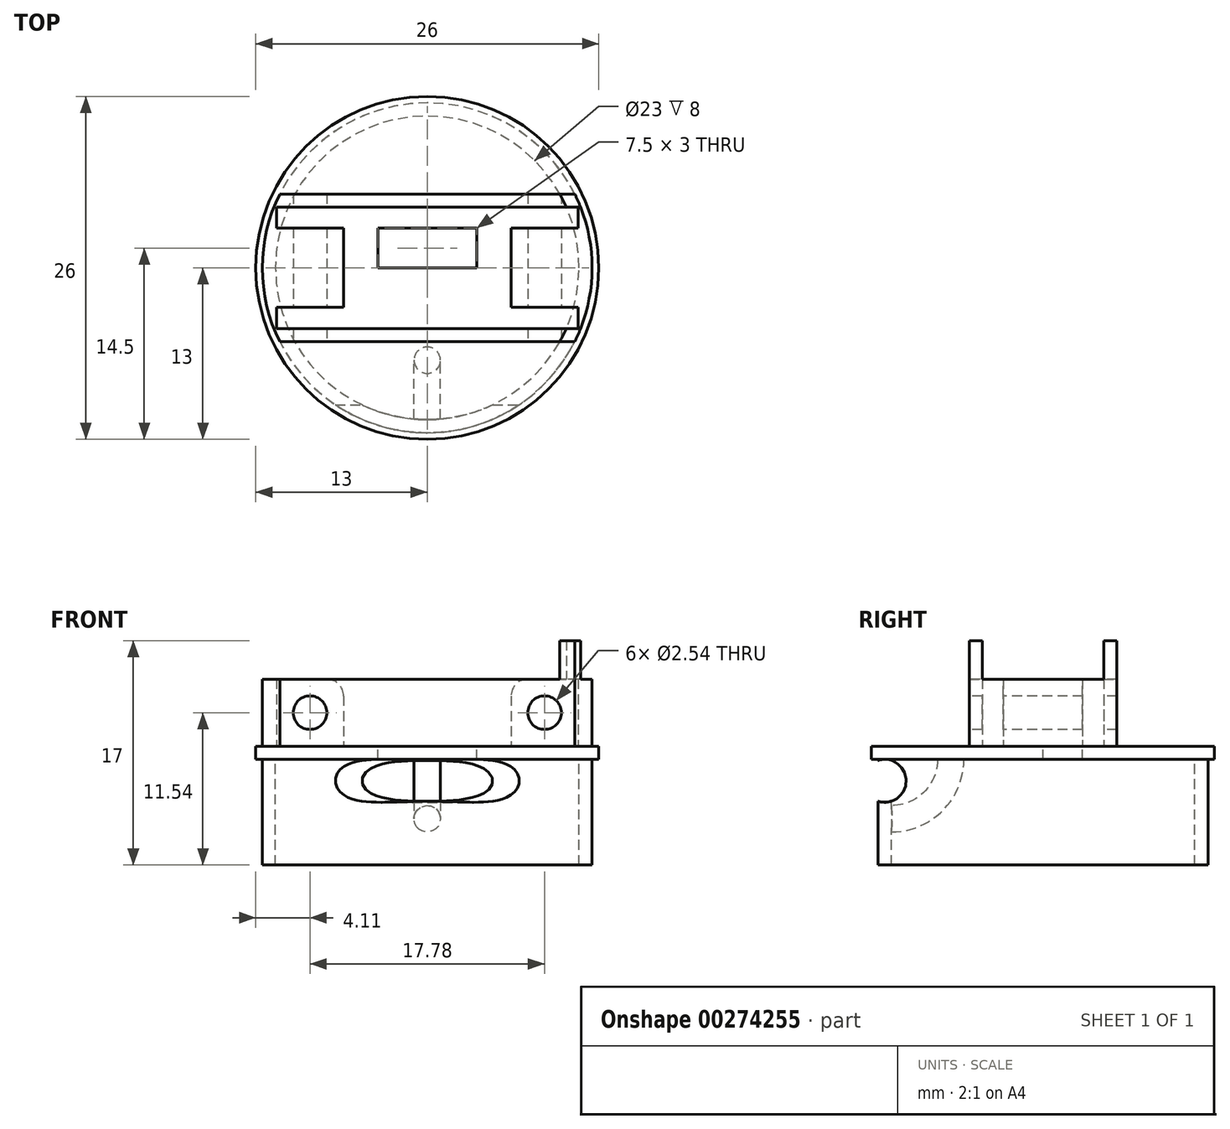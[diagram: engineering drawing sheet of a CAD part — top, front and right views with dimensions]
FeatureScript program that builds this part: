
annotation { "Feature Type Name" : "Feature", "Feature Type Description" : "" }
export const myFeature = defineFeature(function(context is Context, id is Id, definition is map)
    precondition{}
    {
        {
            var Q0;
            Q0=qCreatedBy(makeId("Top.planeOp"),FACE);
            var sketch = newSketch(context, id + "F0", { "sketchPlane" : qUnion([Q0])});
            skCircle(sketch, "E0", {"center": v(0, 0) * mm, "radius": 4.6 * mm, "construction": true});
            skLineSegment(sketch, "E1", {"start": v(11.62, -4.6) * mm, "end": v(11.43, -4.6) * mm});
            skLineSegment(sketch, "E2", {"start": v(-11.62, 4.6) * mm, "end": v(-11.43, 4.6) * mm});
            skCircle(sketch, "E3", {"center": v(0, 0) * mm, "radius": 12.5 * mm});
            skLineSegment(sketch, "E4", {"start": v(0, 0) * mm, "end": v(3.75, 0) * mm});
            skLineSegment(sketch, "E5", {"start": v(0, 0) * mm, "end": v(-3.75, 0) * mm});
            skLineSegment(sketch, "E6", {"start": v(11.43, 3) * mm, "end": v(-11.43, 3) * mm});
            skLineSegment(sketch, "E7", {"start": v(-11.43, 3) * mm, "end": v(-11.43, 0) * mm});
            skLineSegment(sketch, "E8", {"start": v(-11.43, 3) * mm, "end": v(-11.43, 4.6) * mm});
            skLineSegment(sketch, "E9", {"start": v(11.43, 3) * mm, "end": v(11.43, 0) * mm});
            skLineSegment(sketch, "E10", {"start": v(11.43, 3) * mm, "end": v(11.43, 4.6) * mm});
            skLineSegment(sketch, "E11", {"start": v(11.43, 0) * mm, "end": v(11.43, -3) * mm});
            skLineSegment(sketch, "E12", {"start": v(11.43, -3) * mm, "end": v(11.43, -4.6) * mm});
            skLineSegment(sketch, "E13", {"start": v(11.43, -3) * mm, "end": v(6.35, -3) * mm});
            skLineSegment(sketch, "E14", {"start": v(-11.43, -3) * mm, "end": v(-11.43, 0) * mm});
            skLineSegment(sketch, "E15", {"start": v(-11.43, -3) * mm, "end": v(-11.43, -4.6) * mm});
            skLineSegment(sketch, "E16", {"start": v(-11.18, -5.6) * mm, "end": v(11.18, -5.6) * mm});
            skLineSegment(sketch, "E17", {"start": v(-11.18, 5.6) * mm, "end": v(11.18, 5.6) * mm});
            skCircle(sketch, "E18", {"center": v(0, 0) * mm, "radius": 11.5 * mm});
            skCircle(sketch, "E19", {"center": v(0, 0) * mm, "radius": 13 * mm});
            skLineSegment(sketch, "E20", {"start": v(-3.75, 3) * mm, "end": v(-3.75, 0) * mm});
            skLineSegment(sketch, "E21", {"start": v(3.75, 0) * mm, "end": v(3.75, 3) * mm});
            skLineSegment(sketch, "E22", {"start": v(6.35, 3) * mm, "end": v(6.35, 0) * mm});
            skLineSegment(sketch, "E23", {"start": v(-6.35, 3) * mm, "end": v(-6.35, 0) * mm});
            skLineSegment(sketch, "E24", {"start": v(0, -3) * mm, "end": v(-6.35, -3) * mm});
            skLineSegment(sketch, "E25", {"start": v(6.35, -3) * mm, "end": v(6.35, -3) * mm});
            skLineSegment(sketch, "E26", {"start": v(-6.35, -3) * mm, "end": v(-11.43, -3) * mm});
            skLineSegment(sketch, "E27", {"start": v(6.35, -3) * mm, "end": v(0, -3) * mm});
            skLineSegment(sketch, "E28", {"start": v(3.75, 0) * mm, "end": v(6.35, 0) * mm});
            skLineSegment(sketch, "E29", {"start": v(-3.75, 0) * mm, "end": v(-6.35, 0) * mm});
            skLineSegment(sketch, "E30", {"start": v(6.35, 0) * mm, "end": v(6.35, -3) * mm});
            skLineSegment(sketch, "E31", {"start": v(6.35, 0) * mm, "end": v(11.43, 0) * mm});
            skLineSegment(sketch, "E32", {"start": v(-6.35, 0) * mm, "end": v(-6.35, -3) * mm});
            skLineSegment(sketch, "E33", {"start": v(-6.35, 0) * mm, "end": v(-11.43, 0) * mm});
            skLineSegment(sketch, "E34", {"start": v(11.43, 4.6) * mm, "end": v(11.43, 4.6) * mm});
            skLineSegment(sketch, "E35", {"start": v(-11.43, 4.6) * mm, "end": v(11.43, 4.6) * mm});
            skLineSegment(sketch, "E36", {"start": v(-11.43, -4.6) * mm, "end": v(-11.43, -4.6) * mm});
            skLineSegment(sketch, "E37", {"start": v(11.43, -4.6) * mm, "end": v(11.43, -4.6) * mm});
            skLineSegment(sketch, "E38", {"start": v(11.43, -4.6) * mm, "end": v(-11.43, -4.6) * mm});
            skLineSegment(sketch, "E39", {"start": v(11.43, 4.6) * mm, "end": v(11.62, 4.6) * mm});
            skLineSegment(sketch, "E40", {"start": v(-11.43, 4.6) * mm, "end": v(-11.43, 4.6) * mm});
            skLineSegment(sketch, "E41", {"start": v(-11.43, -4.6) * mm, "end": v(-11.62, -4.6) * mm});
            skSolve(sketch);
        }
        {
            var Q0;
            {var subQ0=sQuery(id+"F0.wireOp",EDGE,"E17");var subQ1=sQuery(id+"F0.wireOp",EDGE,"E3");var subQ2=makeQuery(id+"F0.imprint","INTERSECT",VERTEX,{"disambiguationData":[OD(0.0)],"derivedFrom":[subQ1,subQ0]});Q0=makeQuery(id+"F0.imprint","IMPRINT",FACE,{"disambiguationData":[TD([[makeQuery(id+"F0.imprint","IMPRINT",EDGE,{"disambiguationData":[TD([[subQ2,1.0]])],"derivedFrom":subQ1}),1.0]])]});}
            var Q1;
            {var subQ0=sQuery(id+"F0.wireOp",EDGE,"E16");var subQ1=sQuery(id+"F0.wireOp",EDGE,"E3");var subQ2=makeQuery(id+"F0.imprint","INTERSECT",VERTEX,{"disambiguationData":[OD(0.0)],"derivedFrom":[subQ1,subQ0]});Q1=makeQuery(id+"F0.imprint","IMPRINT",FACE,{"disambiguationData":[TD([[makeQuery(id+"F0.imprint","IMPRINT",EDGE,{"disambiguationData":[TD([[subQ2,-1.0]])],"derivedFrom":subQ1}),1.0]])]});}
            extrude(context, id + "F1", {"entities" : qUnion([Q0, Q1]), "depth" : 8 * mm});
        }
        {
            var Q0;
            {var subQ0=sQuery(id+"F0.wireOp",EDGE,"E18");var subQ1=sQuery(id+"F0.wireOp",EDGE,"E16");var subQ2=makeQuery(id+"F0.imprint","INTERSECT",VERTEX,{"disambiguationData":[OD(0.0)],"derivedFrom":[subQ1,subQ0]});Q0=makeQuery(id+"F0.imprint","IMPRINT",FACE,{"disambiguationData":[TD([[makeQuery(id+"F0.imprint","IMPRINT",EDGE,{"disambiguationData":[TD([[subQ2,-1.0]])],"derivedFrom":subQ1}),1.0]])]});}
            var Q1;
            {var subQ0=sQuery(id+"F0.wireOp",EDGE,"E18");var subQ1=sQuery(id+"F0.wireOp",EDGE,"E17");var subQ2=makeQuery(id+"F0.imprint","INTERSECT",VERTEX,{"disambiguationData":[OD(0.0)],"derivedFrom":[subQ1,subQ0]});Q1=makeQuery(id+"F0.imprint","IMPRINT",FACE,{"disambiguationData":[TD([[makeQuery(id+"F0.imprint","IMPRINT",EDGE,{"disambiguationData":[TD([[subQ2,-1.0]])],"derivedFrom":subQ1}),-1.0]])]});}
            var Q2;
            {var subQ5=sQuery(id+"F0.wireOp",EDGE,"E30");Q2=makeQuery(id+"F0.imprint","IMPRINT",FACE,{"disambiguationData":[TD([[makeQuery(id+"F0.imprint","IMPRINT",EDGE,{"derivedFrom":subQ5}),1.0]])]});}
            var Q3;
            {var subQ5=sQuery(id+"F0.wireOp",EDGE,"E22");Q3=makeQuery(id+"F0.imprint","IMPRINT",FACE,{"disambiguationData":[TD([[makeQuery(id+"F0.imprint","IMPRINT",EDGE,{"derivedFrom":subQ5}),1.0]])]});}
            var Q4;
            {var subQ1=sQuery(id+"F0.wireOp",EDGE,"E6");var subQ3=sQuery(id+"F0.wireOp",EDGE,"E18");var subQ4=makeQuery(id+"F0.imprint","INTERSECT",VERTEX,{"disambiguationData":[OD(0.0)],"derivedFrom":[subQ1,subQ3]});Q4=makeQuery(id+"F0.imprint","IMPRINT",FACE,{"disambiguationData":[TD([[makeQuery(id+"F0.imprint","IMPRINT",EDGE,{"disambiguationData":[TD([[subQ4,1.0]])],"derivedFrom":subQ3}),-1.0]])]});}
            var Q5;
            {var subQ1=sQuery(id+"F0.wireOp",EDGE,"E11");var subQ3=sQuery(id+"F0.wireOp",EDGE,"E18");var subQ4=makeQuery(id+"F0.imprint","INTERSECT",VERTEX,{"derivedFrom":[subQ1,subQ3]});Q5=makeQuery(id+"F0.imprint","IMPRINT",FACE,{"disambiguationData":[TD([[makeQuery(id+"F0.imprint","IMPRINT",EDGE,{"disambiguationData":[TD([[subQ4,1.0]])],"derivedFrom":subQ3}),-1.0]])]});}
            var Q6;
            {var subQ1=sQuery(id+"F0.wireOp",EDGE,"E14");var subQ3=sQuery(id+"F0.wireOp",EDGE,"E18");var subQ4=makeQuery(id+"F0.imprint","INTERSECT",VERTEX,{"derivedFrom":[subQ1,subQ3]});Q6=makeQuery(id+"F0.imprint","IMPRINT",FACE,{"disambiguationData":[TD([[makeQuery(id+"F0.imprint","IMPRINT",EDGE,{"disambiguationData":[TD([[subQ4,-1.0]])],"derivedFrom":subQ3}),-1.0]])]});}
            var Q7;
            {var subQ0=sQuery(id+"F0.wireOp",EDGE,"E32");Q7=makeQuery(id+"F0.imprint","IMPRINT",FACE,{"disambiguationData":[TD([[makeQuery(id+"F0.imprint","IMPRINT",EDGE,{"derivedFrom":subQ0}),-1.0]])]});}
            var Q8;
            {var subQ1=sQuery(id+"F0.wireOp",EDGE,"E6");var subQ3=sQuery(id+"F0.wireOp",EDGE,"E18");var subQ4=makeQuery(id+"F0.imprint","INTERSECT",VERTEX,{"disambiguationData":[OD(1.0)],"derivedFrom":[subQ1,subQ3]});Q8=makeQuery(id+"F0.imprint","IMPRINT",FACE,{"disambiguationData":[TD([[makeQuery(id+"F0.imprint","IMPRINT",EDGE,{"disambiguationData":[TD([[subQ4,-1.0]])],"derivedFrom":subQ3}),-1.0]])]});}
            var Q9;
            {var subQ6=sQuery(id+"F0.wireOp",EDGE,"E23");Q9=makeQuery(id+"F0.imprint","IMPRINT",FACE,{"disambiguationData":[TD([[makeQuery(id+"F0.imprint","IMPRINT",EDGE,{"derivedFrom":subQ6}),-1.0]])]});}
            var Q10;
            {var subQ2=sQuery(id+"F0.wireOp",EDGE,"E2");Q10=makeQuery(id+"F0.imprint","IMPRINT",FACE,{"disambiguationData":[TD([[makeQuery(id+"F0.imprint","IMPRINT",EDGE,{"derivedFrom":subQ2}),-1.0]])]});}
            var Q11;
            {var subQ7=sQuery(id+"F0.wireOp",EDGE,"E1");Q11=makeQuery(id+"F0.imprint","IMPRINT",FACE,{"disambiguationData":[TD([[makeQuery(id+"F0.imprint","IMPRINT",EDGE,{"derivedFrom":subQ7}),-1.0]])]});}
            var Q12;
            {var subQ1=sQuery(id+"F0.wireOp",EDGE,"E9");var subQ3=sQuery(id+"F0.wireOp",EDGE,"E18");var subQ4=makeQuery(id+"F0.imprint","INTERSECT",VERTEX,{"derivedFrom":[subQ1,subQ3]});Q12=makeQuery(id+"F0.imprint","IMPRINT",FACE,{"disambiguationData":[TD([[makeQuery(id+"F0.imprint","IMPRINT",EDGE,{"disambiguationData":[TD([[subQ4,1.0]])],"derivedFrom":subQ3}),1.0]])]});}
            var Q13;
            {var subQ1=sQuery(id+"F0.wireOp",EDGE,"E7");var subQ3=sQuery(id+"F0.wireOp",EDGE,"E18");var subQ4=makeQuery(id+"F0.imprint","INTERSECT",VERTEX,{"derivedFrom":[subQ1,subQ3]});Q13=makeQuery(id+"F0.imprint","IMPRINT",FACE,{"disambiguationData":[TD([[makeQuery(id+"F0.imprint","IMPRINT",EDGE,{"disambiguationData":[TD([[subQ4,-1.0]])],"derivedFrom":subQ3}),1.0]])]});}
            var Q14;
            {var subQ1=sQuery(id+"F0.wireOp",EDGE,"E2");Q14=makeQuery(id+"F0.imprint","IMPRINT",FACE,{"disambiguationData":[TD([[makeQuery(id+"F0.imprint","IMPRINT",EDGE,{"derivedFrom":subQ1}),1.0]])]});}
            var Q15;
            {var subQ0=sQuery(id+"F0.wireOp",EDGE,"E41");Q15=makeQuery(id+"F0.imprint","IMPRINT",FACE,{"disambiguationData":[TD([[makeQuery(id+"F0.imprint","IMPRINT",EDGE,{"derivedFrom":subQ0}),1.0]])]});}
            var Q16;
            {var subQ7=sQuery(id+"F0.wireOp",EDGE,"E1");Q16=makeQuery(id+"F0.imprint","IMPRINT",FACE,{"disambiguationData":[TD([[makeQuery(id+"F0.imprint","IMPRINT",EDGE,{"derivedFrom":subQ7}),1.0]])]});}
            var Q17;
            {var subQ0=sQuery(id+"F0.wireOp",EDGE,"E39");Q17=makeQuery(id+"F0.imprint","IMPRINT",FACE,{"disambiguationData":[TD([[makeQuery(id+"F0.imprint","IMPRINT",EDGE,{"derivedFrom":subQ0}),1.0]])]});}
            extrude(context, id + "F2", {"entities" : qUnion([Q0, Q1, Q2, Q3, Q4, Q5, Q6, Q7, Q8, Q9, Q10, Q11, Q12, Q13, Q14, Q15, Q16, Q17]), "operationType" : NewBodyOperationType.ADD, "depth" : 5.08 * mm});
        }
        {
            var Q0;
            Q0=qCreatedBy(makeId("Top.planeOp"),FACE);
            var sketch = newSketch(context, id + "F3", { "sketchPlane" : qUnion([Q0])});
            skCircle(sketch, "E42", {"center": v(0, 0) * mm, "radius": 12.5 * mm});
            skCircle(sketch, "E43", {"center": v(0, 0) * mm, "radius": 11.5 * mm});
            skCircle(sketch, "E44", {"center": v(0, 0) * mm, "radius": 13 * mm});
            skSolve(sketch);
        }
        {
            var Q0;
            Q0=makeQuery(id+"F3.imprint","IMPRINT",FACE,{"disambiguationData":[TD([[makeQuery(id+"F3.imprint","IMPRINT",EDGE,{"derivedFrom":sQuery(id+"F3.wireOp",EDGE,"E42")}),-1.0]])]});
            var Q1;
            Q1=makeQuery(id+"F3.imprint","IMPRINT",FACE,{"disambiguationData":[TD([[makeQuery(id+"F3.imprint","IMPRINT",EDGE,{"derivedFrom":sQuery(id+"F3.wireOp",EDGE,"E43")}),1.0]])]});
            var Q2;
            Q2=makeQuery(id+"F3.imprint","IMPRINT",FACE,{"disambiguationData":[TD([[makeQuery(id+"F3.imprint","IMPRINT",EDGE,{"derivedFrom":sQuery(id+"F3.wireOp",EDGE,"E42")}),1.0]])]});
            extrude(context, id + "F4", {"entities" : qUnion([Q0, Q1, Q2]), "operationType" : NewBodyOperationType.ADD, "oppositeDirection" : true, "depth" : 1 * mm});
        }
        {
            var Q0;
            Q0=makeQuery(id+"F3.imprint","IMPRINT",FACE,{"disambiguationData":[TD([[makeQuery(id+"F3.imprint","IMPRINT",EDGE,{"derivedFrom":sQuery(id+"F3.wireOp",EDGE,"E42")}),1.0]])]});
            extrude(context, id + "F5", {"entities" : qUnion([Q0]), "operationType" : NewBodyOperationType.ADD, "oppositeDirection" : true, "depth" : 9 * mm});
        }
        {
            var Q0;
            Q0=makeQuery(id+"F0.imprint","IMPRINT",FACE,{"disambiguationData":[TD([[makeQuery(id+"F0.imprint","IMPRINT",EDGE,{"derivedFrom":sQuery(id+"F0.wireOp",EDGE,"E4")}),1.0]])]});
            extrude(context, id + "F6", {"entities" : qUnion([Q0]), "operationType" : NewBodyOperationType.REMOVE, "endBound" : BoundingType.THROUGH_ALL, "oppositeDirection" : true, "depth" : 25 * mm});
        }
        {
            var Q0;
            Q0=qCreatedBy(makeId("Right.planeOp"),FACE);
            var sketch = newSketch(context, id + "F7", { "sketchPlane" : qUnion([Q0])});
            skCircle(sketch, "E45", {"center": v(-12, -2.62) * mm, "radius": 1.63 * mm});
            skLineSegment(sketch, "E46", {"start": v(-12, -2.62) * mm, "end": v(-12, 0) * mm, "construction": true});
            skSolve(sketch);
        }
        {
            var Q0;
            Q0 = qSketchRegion(id + "F7", true);
            extrude(context, id + "F8", {"entities" : qUnion([Q0]), "operationType" : NewBodyOperationType.REMOVE, "endBound" : BoundingType.SYMMETRIC, "oppositeDirection" : true, "depth" : 25 * mm});
        }
        {
            var Q0;
            Q0=makeQuery(id+"F4.boolean.opBoolean","SPLIT",FACE,{"disambiguationData":[TD([makeQuery(id+"F5.opExtrude","SWEPT_FACE",FACE,{"disambiguationData":[OSD([sQuery(id+"F3.wireOp",EDGE,"E43")])]})])],"derivedFrom":makeQuery(id+"F4.opExtrude","CAP_FACE",FACE,{"disambiguationData":[OSD([sQuery(id+"F3.wireOp",EDGE,"E44")])],"isStart":false})});
            var sketch = newSketch(context, id + "F9", { "sketchPlane" : qUnion([Q0])});
            skLineSegment(sketch, "E47.bottom", {"start": v(0.75, 11.5) * mm, "end": v(-0.75, 11.5) * mm});
            skPoint(sketch, "E47.middle", {"position": v(0, 9.5) * mm});
            skCircle(sketch, "E48", {"center": v(0, 7) * mm, "radius": 1 * mm});
            skLineSegment(sketch, "E49", {"start": v(0, 7) * mm, "end": v(0, 11.5) * mm, "construction": true});
            skSolve(sketch);
        }
        {
            var Q0;
            Q0 = qSketchRegion(id + "F9", true);
            var Q1;
            Q1=sQuery(id+"F9.wireOp",EDGE,"E47.bottom");
            revolve(context, id + "F10", {"operationType" : NewBodyOperationType.ADD, "entities" : qUnion([Q0]), "axis" : qUnion([Q1]), "revolveType" : RevolveType.ONE_DIRECTION, "angle" : 90 * degree});
        }
        {
            var Q0;
            Q0=qCreatedBy(makeId("Front.planeOp"),FACE);
            var sketch = newSketch(context, id + "F11", { "sketchPlane" : qUnion([Q0])});
            skLineSegment(sketch, "E50", {"start": v(-8.9, 0) * mm, "end": v(-8.9, 2.54) * mm, "construction": true});
            skLineSegment(sketch, "E51", {"start": v(-8.9, 0) * mm, "end": v(0, 0) * mm, "construction": true});
            skLineSegment(sketch, "E52", {"start": v(8.9, 0) * mm, "end": v(8.9, 2.54) * mm, "construction": true});
            skCircle(sketch, "E53", {"center": v(8.9, 2.54) * mm, "radius": 1.27 * mm});
            skCircle(sketch, "E54", {"center": v(-8.9, 2.54) * mm, "radius": 1.27 * mm});
            skCircle(sketch, "E55", {"center": v(-8.9, 2.54) * mm, "radius": 2.54 * mm, "construction": true});
            skCircle(sketch, "E56", {"center": v(8.9, 2.54) * mm, "radius": 2.54 * mm, "construction": true});
            skLineSegment(sketch, "E57", {"start": v(0, 0) * mm, "end": v(8.9, 0) * mm, "construction": true});
            skSolve(sketch);
        }
        {
            var Q0;
            Q0=makeQuery(id+"F11.imprint","IMPRINT",FACE,{"disambiguationData":[TD([[makeQuery(id+"F11.imprint","IMPRINT",EDGE,{"derivedFrom":sQuery(id+"F11.wireOp",EDGE,"E54")}),1.0]])]});
            var Q1;
            Q1=makeQuery(id+"F11.imprint","IMPRINT",FACE,{"disambiguationData":[TD([[makeQuery(id+"F11.imprint","IMPRINT",EDGE,{"derivedFrom":sQuery(id+"F11.wireOp",EDGE,"E53")}),1.0]])]});
            extrude(context, id + "F12", {"entities" : qUnion([Q0, Q1]), "operationType" : NewBodyOperationType.REMOVE, "endBound" : BoundingType.SYMMETRIC, "oppositeDirection" : true, "depth" : 50 * mm});
        }
        {
            var Q0;
            Q0=makeQuery(id+"F2.opExtrude","CAP_EDGE",EDGE,{"disambiguationData":[OSD([sQuery(id+"F0.wireOp",EDGE,"E22"),sQuery(id+"F0.wireOp",EDGE,"E30")])],"isStart":false});
            var Q1;
            Q1=makeQuery(id+"F2.opExtrude","CAP_EDGE",EDGE,{"disambiguationData":[OSD([sQuery(id+"F0.wireOp",EDGE,"E23"),sQuery(id+"F0.wireOp",EDGE,"E32")])],"isStart":false});
            fillet(context, id + "F13", {"entities" : qUnion([Q0, Q1]), "radius" : 1.27 * mm, "tangentPropagation" : true, "allowEdgeOverflow" : false});
        }
        {
            var Q0;
            Q0=makeQuery(id+"F3.imprint","IMPRINT",FACE,{"disambiguationData":[TD([[makeQuery(id+"F3.imprint","IMPRINT",EDGE,{"derivedFrom":sQuery(id+"F3.wireOp",EDGE,"E43")}),1.0]])]});
            var sketch = newSketch(context, id + "F14", { "sketchPlane" : qUnion([Q0])});
            skLineSegment(sketch, "E58", {"start": v(0, 12) * mm, "end": v(0.5, 12.5) * mm});
            skLineSegment(sketch, "E59", {"start": v(0.5, 12.5) * mm, "end": v(-0.5, 12.5) * mm});
            skLineSegment(sketch, "E60", {"start": v(-0.5, 12.5) * mm, "end": v(0, 12) * mm});
            skLineSegment(sketch, "E61", {"start": v(0, -11.5) * mm, "end": v(0, 12.5) * mm, "construction": true});
            skSolve(sketch);
        }
        {
            var Q0;
            Q0 = qSketchRegion(id + "F14", true);
            extrude(context, id + "F15", {"entities" : qUnion([Q0]), "operationType" : NewBodyOperationType.REMOVE, "endBound" : BoundingType.THROUGH_ALL, "depth" : 25 * mm});
        }
    });
